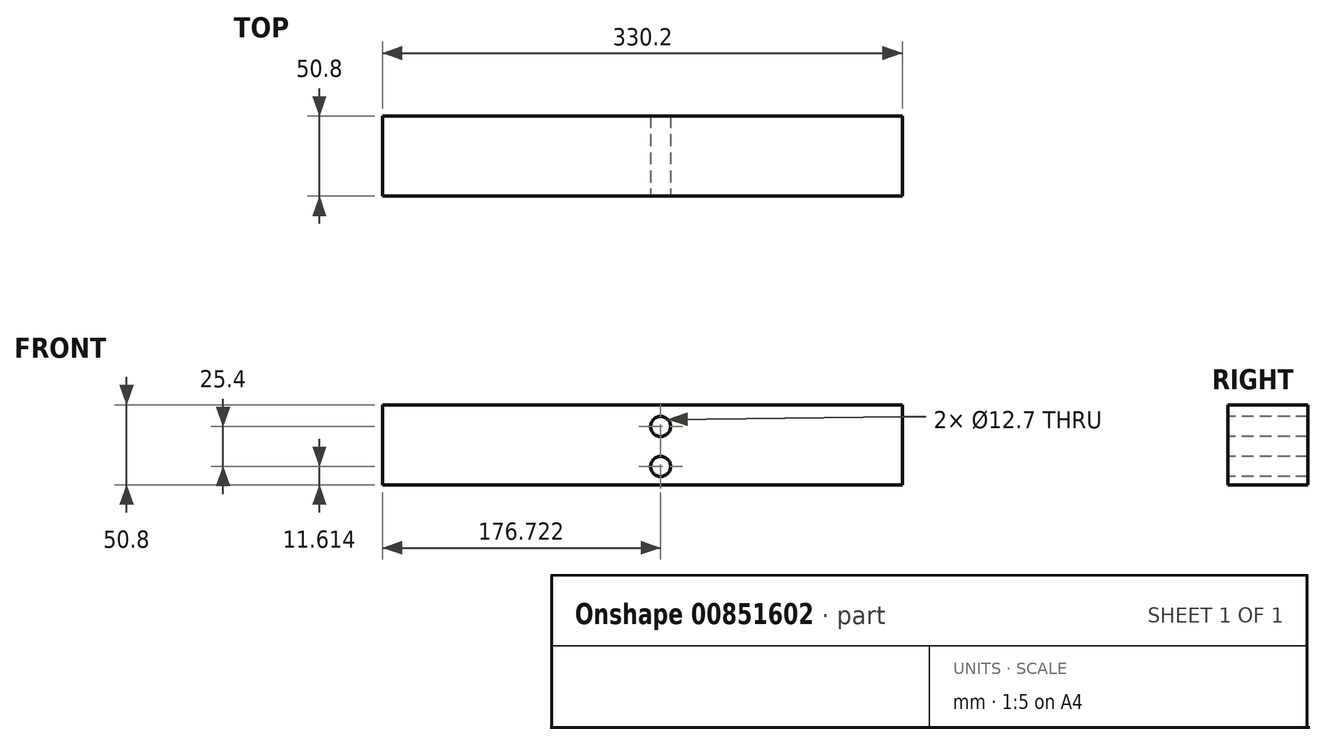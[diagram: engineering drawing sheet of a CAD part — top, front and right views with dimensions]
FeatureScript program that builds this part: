
annotation { "Feature Type Name" : "Feature", "Feature Type Description" : "" }
export const myFeature = defineFeature(function(context is Context, id is Id, definition is map)
    precondition{}
    {
        {
            var Q0;
            Q0=qCreatedBy(makeId("Front.planeOp"),FACE);
            var sketch = newSketch(context, id + "F0", { "sketchPlane" : qUnion([Q0])});
            skLineSegment(sketch, "E0", {"start": v(128.91, 25.49) * mm, "end": v(-201.29, 25.49) * mm});
            skLineSegment(sketch, "E1", {"start": v(-201.29, 25.49) * mm, "end": v(-201.29, -25.31) * mm});
            skLineSegment(sketch, "E2", {"start": v(128.91, 25.49) * mm, "end": v(128.91, -25.31) * mm});
            skLineSegment(sketch, "E3", {"start": v(128.91, -25.31) * mm, "end": v(-201.29, -25.31) * mm});
            skSolve(sketch);
        }
        {
            var Q0;
            Q0=qSketchRegion(id+"F0",true);
            extrude(context, id + "F1", {"entities" : qUnion([Q0]), "depth" : 50.8 * mm, "offsetDistance" : 25.4 * mm});
        }
        {
            var Q0;
            Q0=makeQuery(id+"F1.opExtrude","CAP_FACE",FACE,{"disambiguationData":[OSD([sQuery(id+"F0.wireOp",EDGE,"E0"),sQuery(id+"F0.wireOp",EDGE,"E1"),sQuery(id+"F0.wireOp",EDGE,"E2"),sQuery(id+"F0.wireOp",EDGE,"E3")])],"isStart":false});
            var sketch = newSketch(context, id + "F2", { "sketchPlane" : qUnion([Q0])});
            skCircle(sketch, "E4", {"center": v(-24.57, 11.7) * mm, "radius": 6.35 * mm});
            skCircle(sketch, "E5", {"center": v(-24.57, -13.7) * mm, "radius": 6.35 * mm});
            skSolve(sketch);
        }
        {
            var Q0;
            Q0=qSketchRegion(id+"F2",true);
            extrude(context, id + "F3", {"entities" : qUnion([Q0]), "operationType" : NewBodyOperationType.REMOVE, "oppositeDirection" : true, "depth" : 50.8 * mm, "offsetDistance" : 25.4 * mm});
        }
    });
